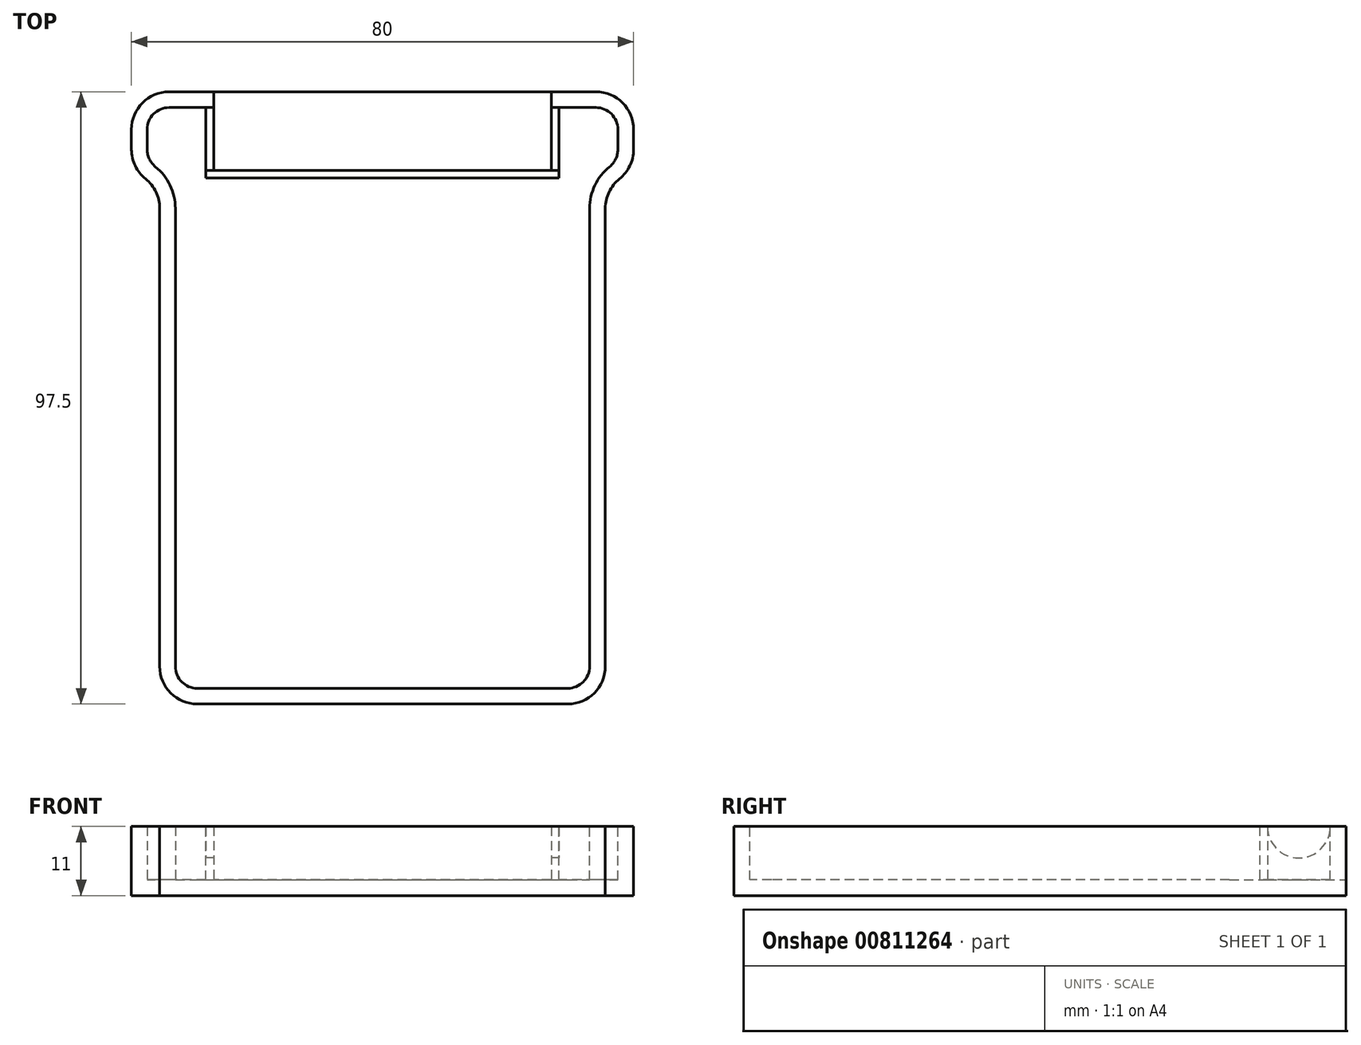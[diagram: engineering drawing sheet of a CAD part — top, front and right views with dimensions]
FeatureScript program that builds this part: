
annotation { "Feature Type Name" : "Feature", "Feature Type Description" : "" }
export const myFeature = defineFeature(function(context is Context, id is Id, definition is map)
    precondition{}
    {
        {
            assignVariable(context, id + "F0", {"name" : "WallThickness", "anyValue" : 2.5});
        }
        {
            assignVariable(context, id + "F1", {"name" : "SensorWidth", "anyValue" : 75});
        }
        {
            assignVariable(context, id + "F2", {"name" : "Depth", "anyValue" : 8.5});
        }
        {
            var Q0;
            Q0=qCreatedBy(makeId("Top.planeOp"),FACE);
            var sketch = newSketch(context, id + "F3", { "sketchPlane" : qUnion([Q0])});
            skLineSegment(sketch, "E0", {"start": v(-35.5, -48.75) * mm, "end": v(35.5, -48.75) * mm});
            skLineSegment(sketch, "E1", {"start": v(35.5, -48.75) * mm, "end": v(35.5, 33.75) * mm});
            skLineSegment(sketch, "E2", {"start": v(35.5, 33.75) * mm, "end": v(40, 33.75) * mm});
            skLineSegment(sketch, "E3", {"start": v(40, 33.75) * mm, "end": v(40, 48.75) * mm});
            skLineSegment(sketch, "E4", {"start": v(40, 48.75) * mm, "end": v(-40, 48.75) * mm});
            skLineSegment(sketch, "E5", {"start": v(-40, 48.75) * mm, "end": v(-40, 33.75) * mm});
            skLineSegment(sketch, "E6", {"start": v(-40, 33.75) * mm, "end": v(-35.5, 33.75) * mm});
            skLineSegment(sketch, "E7", {"start": v(-35.5, 33.75) * mm, "end": v(-35.5, -48.75) * mm});
            skLineSegment(sketch, "E8", {"start": v(-35.5, 33.75) * mm, "end": v(35.5, 33.75) * mm, "construction": true});
            skLineSegment(sketch, "E9", {"start": v(-35.5, 33.75) * mm, "end": v(-35.5, 48.75) * mm, "construction": true});
            skSolve(sketch);
        }
        {
            var Q0;
            Q0=makeQuery(id+"F3.imprint","IMPRINT",FACE,{"disambiguationData":[TD([[makeQuery(id+"F3.imprint","IMPRINT",EDGE,{"derivedFrom":sQuery(id+"F3.wireOp",EDGE,"E0")}),1.0]])]});
            extrude(context, id + "F4", {"entities" : qUnion([Q0]), "depth" : (getVariable(context, 'Depth') + getVariable(context, 'WallThickness')) * mm, "offsetDistance" : 25 * mm});
        }
        {
            var Q0;
            Q0=makeQuery(id+"F4.opExtrude","SWEPT_EDGE",EDGE,{"disambiguationData":[OSD([sQuery(id+"F3.wireOp",EDGE,"E0"),sQuery(id+"F3.wireOp",EDGE,"E7")])]});
            var Q1;
            Q1=makeQuery(id+"F4.opExtrude","SWEPT_EDGE",EDGE,{"disambiguationData":[OSD([sQuery(id+"F3.wireOp",EDGE,"E0"),sQuery(id+"F3.wireOp",EDGE,"E1")])]});
            var Q2;
            Q2=makeQuery(id+"F4.opExtrude","SWEPT_EDGE",EDGE,{"disambiguationData":[OSD([sQuery(id+"F3.wireOp",EDGE,"E3"),sQuery(id+"F3.wireOp",EDGE,"E4")])]});
            var Q3;
            Q3=makeQuery(id+"F4.opExtrude","SWEPT_EDGE",EDGE,{"disambiguationData":[OSD([sQuery(id+"F3.wireOp",EDGE,"E4"),sQuery(id+"F3.wireOp",EDGE,"E5")])]});
            var Q4;
            Q4=makeQuery(id+"F4.opExtrude","SWEPT_EDGE",EDGE,{"disambiguationData":[OSD([sQuery(id+"F3.wireOp",EDGE,"E5"),sQuery(id+"F3.wireOp",EDGE,"E6")])]});
            var Q5;
            Q5=makeQuery(id+"F4.opExtrude","SWEPT_EDGE",EDGE,{"disambiguationData":[OSD([sQuery(id+"F3.wireOp",EDGE,"E2"),sQuery(id+"F3.wireOp",EDGE,"E3")])]});
            fillet(context, id + "F5", {"entities" : qUnion([Q0, Q1, Q2, Q3, Q4, Q5]), "radius" : 6 * mm, "tangentPropagation" : true, "allowEdgeOverflow" : false});
        }
        {
            var Q0;
            Q0=makeQuery(id+"F5.opFillet","BLEND_EDGE",EDGE,{"blendedFrom":[makeQuery(id+"F4.opExtrude","SWEPT_EDGE",EDGE,{"disambiguationData":[OSD([sQuery(id+"F3.wireOp",EDGE,"E2"),sQuery(id+"F3.wireOp",EDGE,"E3")])]}),makeQuery(id+"F4.opExtrude","SWEPT_FACE",FACE,{"disambiguationData":[OSD([sQuery(id+"F3.wireOp",EDGE,"E1")])]})],"blendedInto":[makeQuery(id+"F4.opExtrude","SWEPT_FACE",FACE,{"disambiguationData":[OSD([sQuery(id+"F3.wireOp",EDGE,"E1")])]})]});
            var Q1;
            Q1=makeQuery(id+"F5.opFillet","BLEND_EDGE",EDGE,{"blendedFrom":[makeQuery(id+"F4.opExtrude","SWEPT_EDGE",EDGE,{"disambiguationData":[OSD([sQuery(id+"F3.wireOp",EDGE,"E5"),sQuery(id+"F3.wireOp",EDGE,"E6")])]}),makeQuery(id+"F4.opExtrude","SWEPT_FACE",FACE,{"disambiguationData":[OSD([sQuery(id+"F3.wireOp",EDGE,"E7")])]})],"blendedInto":[makeQuery(id+"F4.opExtrude","SWEPT_FACE",FACE,{"disambiguationData":[OSD([sQuery(id+"F3.wireOp",EDGE,"E7")])]})]});
            fillet(context, id + "F6", {"entities" : qUnion([Q0, Q1]), "radius" : 6 * mm, "tangentPropagation" : true, "allowEdgeOverflow" : false});
        }
        {
            var Q0;
            Q0=makeQuery(id+"F4.opExtrude","CAP_FACE",FACE,{"disambiguationData":[OSD([sQuery(id+"F3.wireOp",EDGE,"E0"),sQuery(id+"F3.wireOp",EDGE,"E1"),sQuery(id+"F3.wireOp",EDGE,"E2"),sQuery(id+"F3.wireOp",EDGE,"E3"),sQuery(id+"F3.wireOp",EDGE,"E4"),sQuery(id+"F3.wireOp",EDGE,"E5"),sQuery(id+"F3.wireOp",EDGE,"E6"),sQuery(id+"F3.wireOp",EDGE,"E7")])],"isStart":false});
            shell(context, id + "F7", {"entities" : qUnion([Q0]), "thickness" : (getVariable(context, 'WallThickness')) * mm});
        }
        {
            var Q0;
            Q0=makeQuery(id+"F4.opExtrude","CAP_FACE",FACE,{"disambiguationData":[OSD([sQuery(id+"F3.wireOp",EDGE,"E0"),sQuery(id+"F3.wireOp",EDGE,"E1"),sQuery(id+"F3.wireOp",EDGE,"E2"),sQuery(id+"F3.wireOp",EDGE,"E3"),sQuery(id+"F3.wireOp",EDGE,"E4"),sQuery(id+"F3.wireOp",EDGE,"E5"),sQuery(id+"F3.wireOp",EDGE,"E6"),sQuery(id+"F3.wireOp",EDGE,"E7")])],"isStart":false});
            var sketch = newSketch(context, id + "F8", { "sketchPlane" : qUnion([Q0])});
            skLineSegment(sketch, "E10.bottom", {"start": v(-28.12, 48.75) * mm, "end": v(28.12, 48.75) * mm});
            skLineSegment(sketch, "E10.top", {"start": v(-28.12, 46.25) * mm, "end": v(28.12, 46.25) * mm});
            skLineSegment(sketch, "E10.left", {"start": v(-28.12, 48.75) * mm, "end": v(-28.12, 46.25) * mm});
            skLineSegment(sketch, "E10.right", {"start": v(28.12, 48.75) * mm, "end": v(28.12, 46.25) * mm});
            skSolve(sketch);
        }
        {
            var Q0;
            Q0 = qSketchRegion(id + "F8", true);
            extrude(context, id + "F9", {"entities" : qUnion([Q0]), "operationType" : NewBodyOperationType.REMOVE, "oppositeDirection" : true, "depth" : (getVariable(context, 'Depth')) * mm, "offsetDistance" : 25 * mm});
        }
        {
            var Q0;
            Q0=makeQuery(id+"F9.boolean.opBoolean","MERGE",FACE,{"derivedFrom":[makeQuery(id+"F7.opShell","OFFSET_FACE",FACE,{"disambiguationData":[OSD([sQuery(id+"F3.wireOp",EDGE,"E0"),sQuery(id+"F3.wireOp",EDGE,"E1"),sQuery(id+"F3.wireOp",EDGE,"E2"),sQuery(id+"F3.wireOp",EDGE,"E3"),sQuery(id+"F3.wireOp",EDGE,"E4"),sQuery(id+"F3.wireOp",EDGE,"E5"),sQuery(id+"F3.wireOp",EDGE,"E6"),sQuery(id+"F3.wireOp",EDGE,"E7")])]}),makeQuery(id+"F9.opExtrude","CAP_FACE",FACE,{"disambiguationData":[OSD([sQuery(id+"F8.wireOp",EDGE,"E10.bottom"),sQuery(id+"F8.wireOp",EDGE,"E10.top"),sQuery(id+"F8.wireOp",EDGE,"E10.left"),sQuery(id+"F8.wireOp",EDGE,"E10.right")])],"isStart":false})]});
            var sketch = newSketch(context, id + "F10", { "sketchPlane" : qUnion([Q0])});
            skLineSegment(sketch, "E11", {"start": v(-28.12, 46.25) * mm, "end": v(-28.12, 35) * mm});
            skLineSegment(sketch, "E12", {"start": v(-28.12, 35) * mm, "end": v(28.12, 35) * mm});
            skLineSegment(sketch, "E13", {"start": v(28.12, 35) * mm, "end": v(28.12, 48.75) * mm});
            skLineSegment(sketch, "E14", {"start": v(28.12, 48.75) * mm, "end": v(26.87, 48.75) * mm});
            skLineSegment(sketch, "E15", {"start": v(26.87, 48.75) * mm, "end": v(26.87, 36.25) * mm});
            skLineSegment(sketch, "E16", {"start": v(26.87, 36.25) * mm, "end": v(-26.87, 36.25) * mm});
            skLineSegment(sketch, "E17", {"start": v(-26.87, 36.25) * mm, "end": v(-26.87, 48.75) * mm});
            skLineSegment(sketch, "E18", {"start": v(-26.87, 48.75) * mm, "end": v(-28.12, 48.75) * mm});
            skLineSegment(sketch, "E19", {"start": v(-28.12, 48.75) * mm, "end": v(-28.12, 46.25) * mm});
            skLineSegment(sketch, "E20", {"start": v(-26.87, 36.25) * mm, "end": v(-26.87, 35) * mm, "construction": true});
            skLineSegment(sketch, "E21", {"start": v(-26.87, 36.25) * mm, "end": v(-28.12, 36.25) * mm, "construction": true});
            skLineSegment(sketch, "E22", {"start": v(26.87, 36.25) * mm, "end": v(28.12, 36.25) * mm, "construction": true});
            skSolve(sketch);
        }
        {
            var Q0;
            Q0 = qSketchRegion(id + "F10", true);
            extrude(context, id + "F11", {"entities" : qUnion([Q0]), "operationType" : NewBodyOperationType.ADD, "depth" : (getVariable(context, 'Depth')) * mm, "offsetDistance" : 25 * mm});
        }
        {
            var Q0;
            Q0=makeQuery(id+"F11.opExtrude","SWEPT_FACE",FACE,{"disambiguationData":[OSD([sQuery(id+"F10.wireOp",EDGE,"E11"),sQuery(id+"F10.wireOp",EDGE,"E19")])]});
            var sketch = newSketch(context, id + "F12", { "sketchPlane" : qUnion([Q0])});
            skCircle(sketch, "E23", {"center": v(-41.25, 11) * mm, "radius": 5 * mm});
            skSolve(sketch);
        }
        {
            var Q0;
            Q0 = qSketchRegion(id + "F12", true);
            extrude(context, id + "F13", {"entities" : qUnion([Q0]), "operationType" : NewBodyOperationType.REMOVE, "oppositeDirection" : true, "depth" : (getVariable(context, 'SensorWidth') * 0.75) * mm, "offsetDistance" : 25 * mm});
        }
    });
